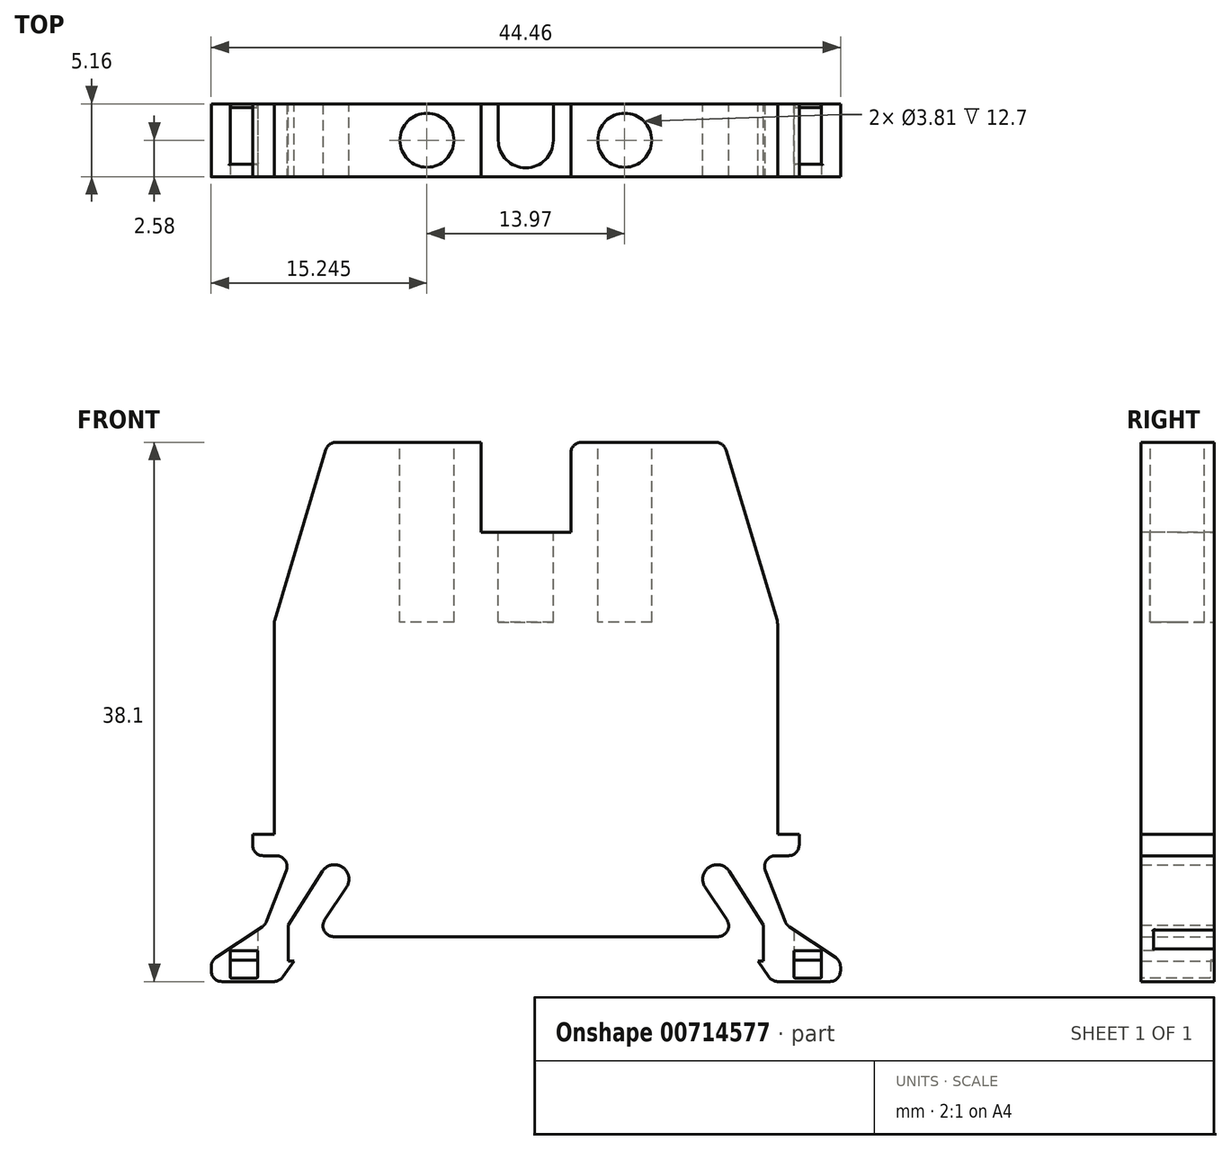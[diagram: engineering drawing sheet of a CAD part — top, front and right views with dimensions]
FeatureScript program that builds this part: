
annotation { "Feature Type Name" : "Feature", "Feature Type Description" : "" }
export const myFeature = defineFeature(function(context is Context, id is Id, definition is map)
    precondition{}
    {
        {
            var Q0;
            Q0=qCreatedBy(makeId("Front.planeOp"),FACE);
            var sketch = newSketch(context, id + "F0", { "sketchPlane" : qUnion([Q0])});
            skLineSegment(sketch, "E0", {"start": v(-13.97, 38.1) * mm, "end": v(13.97, 38.1) * mm});
            skLineSegment(sketch, "E1", {"start": v(0, 38.1) * mm, "end": v(0, 0) * mm, "construction": true});
            skLineSegment(sketch, "E2", {"start": v(-17.78, 25.4) * mm, "end": v(17.78, 25.4) * mm, "construction": true});
            skPoint(sketch, "E3", {"position": v(0, 25.4) * mm});
            skLineSegment(sketch, "E4", {"start": v(-17.78, 25.4) * mm, "end": v(-13.97, 38.1) * mm});
            skLineSegment(sketch, "E5", {"start": v(13.97, 38.1) * mm, "end": v(17.78, 25.4) * mm});
            skLineSegment(sketch, "E6", {"start": v(17.78, 8.9) * mm, "end": v(-17.78, 8.9) * mm});
            skLineSegment(sketch, "E7", {"start": v(17.78, 8.9) * mm, "end": v(19.3, 8.9) * mm});
            skLineSegment(sketch, "E8", {"start": v(19.3, 8.89) * mm, "end": v(19.3, 10.41) * mm});
            skLineSegment(sketch, "E9", {"start": v(19.3, 10.41) * mm, "end": v(17.78, 10.41) * mm});
            skLineSegment(sketch, "E10", {"start": v(17.78, 10.41) * mm, "end": v(17.78, 25.4) * mm});
            skLineSegment(sketch, "E11", {"start": v(-17.78, 8.9) * mm, "end": v(-19.3, 8.9) * mm});
            skLineSegment(sketch, "E12", {"start": v(-19.3, 8.89) * mm, "end": v(-19.3, 10.41) * mm});
            skLineSegment(sketch, "E13", {"start": v(-19.3, 10.41) * mm, "end": v(-17.78, 10.41) * mm});
            skLineSegment(sketch, "E14", {"start": v(-17.78, 10.41) * mm, "end": v(-17.78, 25.4) * mm});
            skLineSegment(sketch, "E15", {"start": v(-18.41, 4) * mm, "end": v(18.41, 4) * mm, "construction": true});
            skPoint(sketch, "E16", {"position": v(0, 4) * mm});
            skLineSegment(sketch, "E17", {"start": v(16.5, 8.89) * mm, "end": v(18.41, 4) * mm});
            skLineSegment(sketch, "E18", {"start": v(-18.41, 4) * mm, "end": v(-16.5, 8.89) * mm});
            skLineSegment(sketch, "E19", {"start": v(-16.51, 8.9) * mm, "end": v(16.51, 8.9) * mm, "construction": true});
            skPoint(sketch, "E20", {"position": v(0, 8.9) * mm});
            skLineSegment(sketch, "E21", {"start": v(-22.23, 1.46) * mm, "end": v(22.23, 1.46) * mm, "construction": true});
            skPoint(sketch, "E22", {"position": v(0, 1.46) * mm});
            skLineSegment(sketch, "E23", {"start": v(-18.41, 4) * mm, "end": v(-22.22, 1.46) * mm});
            skLineSegment(sketch, "E24", {"start": v(-22.23, 1.46) * mm, "end": v(-22.23, 0) * mm});
            skLineSegment(sketch, "E25", {"start": v(-22.23, 0) * mm, "end": v(-17.4, 0) * mm});
            skLineSegment(sketch, "E26", {"start": v(18.41, 4) * mm, "end": v(22.22, 1.46) * mm});
            skLineSegment(sketch, "E27", {"start": v(22.23, 1.46) * mm, "end": v(22.23, 0) * mm});
            skLineSegment(sketch, "E28", {"start": v(-14.99, 3.17) * mm, "end": v(14.99, 3.18) * mm});
            skPoint(sketch, "E29", {"position": v(0, 3.17) * mm});
            skLineSegment(sketch, "E30", {"start": v(-13.51, 7.24) * mm, "end": v(13.51, 7.24) * mm});
            skPoint(sketch, "E31", {"position": v(0, 7.24) * mm});
            skArc(sketch, "E32", {"start": v(-12.67, 6.68) * mm, "mid": v(-12.96, 8.1) * mm, "end": v(-14.37, 7.78) * mm});
            skArc(sketch, "E33", {"start": v(14.37, 7.78) * mm, "mid": v(12.96, 8.1) * mm, "end": v(12.67, 6.68) * mm});
            skLineSegment(sketch, "E34", {"start": v(-14.99, 3.17) * mm, "end": v(-12.67, 6.68) * mm});
            skLineSegment(sketch, "E35", {"start": v(14.99, 3.18) * mm, "end": v(12.67, 6.68) * mm});
            skLineSegment(sketch, "E36", {"start": v(-18.41, 4) * mm, "end": v(-16.76, 4) * mm, "construction": true});
            skLineSegment(sketch, "E37", {"start": v(-16.76, 4) * mm, "end": v(-14.37, 7.78) * mm});
            skLineSegment(sketch, "E38", {"start": v(18.41, 4) * mm, "end": v(16.76, 4) * mm});
            skLineSegment(sketch, "E39", {"start": v(14.37, 7.78) * mm, "end": v(16.76, 4) * mm});
            skLineSegment(sketch, "E40", {"start": v(22.23, 0) * mm, "end": v(17.4, 0) * mm});
            skLineSegment(sketch, "E41", {"start": v(17.4, 0) * mm, "end": v(16.38, 1.46) * mm});
            skLineSegment(sketch, "E42", {"start": v(16.38, 1.46) * mm, "end": v(16.76, 1.46) * mm});
            skLineSegment(sketch, "E43", {"start": v(16.76, 1.46) * mm, "end": v(16.76, 4) * mm});
            skLineSegment(sketch, "E44", {"start": v(-17.4, 0) * mm, "end": v(-16.38, 1.46) * mm});
            skLineSegment(sketch, "E45", {"start": v(-16.38, 1.46) * mm, "end": v(-16.76, 1.46) * mm});
            skLineSegment(sketch, "E46", {"start": v(-16.76, 1.46) * mm, "end": v(-16.76, 4) * mm});
            skSolve(sketch);
        }
        {
            var Q0;
            Q0 = qSketchRegion(id + "F0", true);
            extrude(context, id + "F1", {"entities" : qUnion([Q0]), "depth" : 5.16 * mm, "offsetDistance" : 25.4 * mm});
        }
        {
            var Q0;
            Q0=makeQuery(id+"F1.opExtrude","CAP_FACE",FACE,{"disambiguationData":[OSD([sQuery(id+"F0.wireOp",EDGE,"E0"),sQuery(id+"F0.wireOp",EDGE,"E4"),sQuery(id+"F0.wireOp",EDGE,"E5"),sQuery(id+"F0.wireOp",EDGE,"E6"),sQuery(id+"F0.wireOp",EDGE,"E7"),sQuery(id+"F0.wireOp",EDGE,"E8"),sQuery(id+"F0.wireOp",EDGE,"E9"),sQuery(id+"F0.wireOp",EDGE,"E10"),sQuery(id+"F0.wireOp",EDGE,"E11"),sQuery(id+"F0.wireOp",EDGE,"E12"),sQuery(id+"F0.wireOp",EDGE,"E13"),sQuery(id+"F0.wireOp",EDGE,"E14"),sQuery(id+"F0.wireOp",EDGE,"E17"),sQuery(id+"F0.wireOp",EDGE,"E18"),sQuery(id+"F0.wireOp",EDGE,"E23"),sQuery(id+"F0.wireOp",EDGE,"E24"),sQuery(id+"F0.wireOp",EDGE,"E25"),sQuery(id+"F0.wireOp",EDGE,"E26"),sQuery(id+"F0.wireOp",EDGE,"E27"),sQuery(id+"F0.wireOp",EDGE,"E28"),sQuery(id+"F0.wireOp",EDGE,"E32"),sQuery(id+"F0.wireOp",EDGE,"E33"),sQuery(id+"F0.wireOp",EDGE,"E34"),sQuery(id+"F0.wireOp",EDGE,"E35"),sQuery(id+"F0.wireOp",EDGE,"E37"),sQuery(id+"F0.wireOp",EDGE,"E39"),sQuery(id+"F0.wireOp",EDGE,"E40"),sQuery(id+"F0.wireOp",EDGE,"E41"),sQuery(id+"F0.wireOp",EDGE,"E42"),sQuery(id+"F0.wireOp",EDGE,"E43"),sQuery(id+"F0.wireOp",EDGE,"E44"),sQuery(id+"F0.wireOp",EDGE,"E45"),sQuery(id+"F0.wireOp",EDGE,"E46")])],"isStart":false});
            var sketch = newSketch(context, id + "F2", { "sketchPlane" : qUnion([Q0])});
            skLineSegment(sketch, "E47", {"start": v(-3.18, 38.1) * mm, "end": v(3.17, 38.1) * mm});
            skLineSegment(sketch, "E48", {"start": v(3.17, 38.1) * mm, "end": v(3.17, 31.75) * mm});
            skLineSegment(sketch, "E49", {"start": v(3.17, 31.75) * mm, "end": v(-3.18, 31.75) * mm});
            skLineSegment(sketch, "E50", {"start": v(-3.18, 31.75) * mm, "end": v(-3.18, 38.1) * mm});
            skPoint(sketch, "E51", {"position": v(0, 38.1) * mm});
            skLineSegment(sketch, "E52", {"start": v(-13.97, 38.1) * mm, "end": v(13.97, 38.1) * mm});
            skSolve(sketch);
        }
        {
            var Q0;
            Q0 = qSketchRegion(id + "F2", true);
            extrude(context, id + "F3", {"entities" : qUnion([Q0]), "operationType" : NewBodyOperationType.REMOVE, "oppositeDirection" : true, "depth" : 25.4 * mm, "offsetDistance" : 25.4 * mm});
        }
        {
            var Q0;
            {var subQ30=sQuery(id+"F0.wireOp",EDGE,"E5");var subQ32=sQuery(id+"F0.wireOp",EDGE,"E0");Q0=makeQuery(id+"F3.boolean.opBoolean","SPLIT",FACE,{"disambiguationData":[TD([makeQuery(id+"F1.opExtrude","SWEPT_FACE",FACE,{"disambiguationData":[OSD([subQ30])]})])],"derivedFrom":makeQuery(id+"F1.opExtrude","SWEPT_FACE",FACE,{"disambiguationData":[OSD([subQ32])]})});}
            var sketch = newSketch(context, id + "F4", { "sketchPlane" : qUnion([Q0])});
            skCircle(sketch, "E53", {"center": v(-6.99, -2.58) * mm, "radius": 1.9 * mm});
            skLineSegment(sketch, "E54", {"start": v(-13.97, -5.16) * mm, "end": v(-3.17, 0) * mm, "construction": true});
            skLineSegment(sketch, "E55", {"start": v(3.18, 0) * mm, "end": v(13.97, -5.16) * mm, "construction": true});
            skLineSegment(sketch, "E56", {"start": v(-8.57, -2.58) * mm, "end": v(-6.99, -2.58) * mm, "construction": true});
            skLineSegment(sketch, "E57", {"start": v(-6.99, -2.58) * mm, "end": v(6.99, -2.58) * mm, "construction": true});
            skLineSegment(sketch, "E58", {"start": v(6.99, -2.58) * mm, "end": v(8.57, -2.58) * mm, "construction": true});
            skCircle(sketch, "E59", {"center": v(6.99, -2.58) * mm, "radius": 1.9 * mm});
            skArc(sketch, "E60", {"start": v(-1.94, -2.58) * mm, "mid": v(0, -4.52) * mm, "end": v(1.94, -2.58) * mm});
            skLineSegment(sketch, "E61", {"start": v(-3.17, -5.16) * mm, "end": v(3.18, -5.16) * mm, "construction": true});
            skLineSegment(sketch, "E62", {"start": v(-1.94, -2.58) * mm, "end": v(-1.94, 0) * mm});
            skLineSegment(sketch, "E63", {"start": v(1.94, -2.58) * mm, "end": v(1.94, 0) * mm});
            skLineSegment(sketch, "E64", {"start": v(1.94, 0) * mm, "end": v(-1.94, 0) * mm});
            skSolve(sketch);
        }
        {
            var Q0;
            Q0 = qSketchRegion(id + "F4", true);
            extrude(context, id + "F5", {"entities" : qUnion([Q0]), "operationType" : NewBodyOperationType.REMOVE, "oppositeDirection" : true, "depth" : 12.7 * mm, "offsetDistance" : 25.4 * mm});
        }
        {
            var Q0;
            Q0=makeQuery(id+"F1.opExtrude","SWEPT_EDGE",EDGE,{"disambiguationData":[OSD([sQuery(id+"F0.wireOp",EDGE,"E0"),sQuery(id+"F0.wireOp",EDGE,"E5")])]});
            var Q1;
            Q1=makeQuery(id+"F1.opExtrude","SWEPT_EDGE",EDGE,{"disambiguationData":[OSD([sQuery(id+"F0.wireOp",EDGE,"E0"),sQuery(id+"F0.wireOp",EDGE,"E4")])]});
            var Q2;
            Q2=makeQuery(id+"F1.opExtrude","SWEPT_EDGE",EDGE,{"disambiguationData":[OSD([sQuery(id+"F0.wireOp",EDGE,"E5"),sQuery(id+"F0.wireOp",EDGE,"E10")])]});
            var Q3;
            Q3=makeQuery(id+"F1.opExtrude","SWEPT_EDGE",EDGE,{"disambiguationData":[OSD([sQuery(id+"F0.wireOp",EDGE,"E6"),sQuery(id+"F0.wireOp",EDGE,"E17")])]});
            var Q4;
            Q4=makeQuery(id+"F1.opExtrude","SWEPT_EDGE",EDGE,{"disambiguationData":[OSD([sQuery(id+"F0.wireOp",EDGE,"E7"),sQuery(id+"F0.wireOp",EDGE,"E8")])]});
            var Q5;
            Q5=makeQuery(id+"F1.opExtrude","SWEPT_EDGE",EDGE,{"disambiguationData":[OSD([sQuery(id+"F0.wireOp",EDGE,"E6"),sQuery(id+"F0.wireOp",EDGE,"E18")])]});
            var Q6;
            Q6=makeQuery(id+"F1.opExtrude","SWEPT_EDGE",EDGE,{"disambiguationData":[OSD([sQuery(id+"F0.wireOp",EDGE,"E11"),sQuery(id+"F0.wireOp",EDGE,"E12")])]});
            var Q7;
            Q7=makeQuery(id+"F1.opExtrude","SWEPT_EDGE",EDGE,{"disambiguationData":[OSD([sQuery(id+"F0.wireOp",EDGE,"E28"),sQuery(id+"F0.wireOp",EDGE,"E35")])]});
            var Q8;
            Q8=makeQuery(id+"F1.opExtrude","SWEPT_EDGE",EDGE,{"disambiguationData":[OSD([sQuery(id+"F0.wireOp",EDGE,"E28"),sQuery(id+"F0.wireOp",EDGE,"E34")])]});
            var Q9;
            Q9=makeQuery(id+"F1.opExtrude","SWEPT_EDGE",EDGE,{"disambiguationData":[OSD([sQuery(id+"F0.wireOp",EDGE,"E18"),sQuery(id+"F0.wireOp",EDGE,"E23")])]});
            var Q10;
            Q10=makeQuery(id+"F1.opExtrude","SWEPT_EDGE",EDGE,{"disambiguationData":[OSD([sQuery(id+"F0.wireOp",EDGE,"E23"),sQuery(id+"F0.wireOp",EDGE,"E24")])]});
            var Q11;
            Q11=makeQuery(id+"F1.opExtrude","SWEPT_EDGE",EDGE,{"disambiguationData":[OSD([sQuery(id+"F0.wireOp",EDGE,"E24"),sQuery(id+"F0.wireOp",EDGE,"E25")])]});
            var Q12;
            Q12=makeQuery(id+"F1.opExtrude","SWEPT_EDGE",EDGE,{"disambiguationData":[OSD([sQuery(id+"F0.wireOp",EDGE,"E27"),sQuery(id+"F0.wireOp",EDGE,"E40")])]});
            var Q13;
            Q13=makeQuery(id+"F1.opExtrude","SWEPT_EDGE",EDGE,{"disambiguationData":[OSD([sQuery(id+"F0.wireOp",EDGE,"E26"),sQuery(id+"F0.wireOp",EDGE,"E27")])]});
            var Q14;
            Q14=makeQuery(id+"F1.opExtrude","SWEPT_EDGE",EDGE,{"disambiguationData":[OSD([sQuery(id+"F0.wireOp",EDGE,"E17"),sQuery(id+"F0.wireOp",EDGE,"E26"),sQuery(id+"F0.wireOp",EDGE,"E38")])]});
            var Q15;
            Q15=makeQuery(id+"F1.opExtrude","SWEPT_EDGE",EDGE,{"disambiguationData":[OSD([sQuery(id+"F0.wireOp",EDGE,"E40"),sQuery(id+"F0.wireOp",EDGE,"E41")])]});
            var Q16;
            Q16=makeQuery(id+"F1.opExtrude","SWEPT_EDGE",EDGE,{"disambiguationData":[OSD([sQuery(id+"F0.wireOp",EDGE,"E25"),sQuery(id+"F0.wireOp",EDGE,"E44")])]});
            var Q17;
            Q17=makeQuery(id+"F3.boolean.opBoolean","COPY",EDGE,{"derivedFrom":makeQuery(id+"F3.opExtrude","SWEPT_EDGE",EDGE,{"disambiguationData":[OSD([sQuery(id+"F2.wireOp",EDGE,"E48"),sQuery(id+"F2.wireOp",EDGE,"E52")])]})});
            var Q18;
            Q18=makeQuery(id+"F3.boolean.opBoolean","COPY",EDGE,{"derivedFrom":makeQuery(id+"F3.opExtrude","SWEPT_EDGE",EDGE,{"disambiguationData":[OSD([sQuery(id+"F2.wireOp",EDGE,"E50"),sQuery(id+"F2.wireOp",EDGE,"E52")])]})});
            var Q19;
            Q19=makeQuery(id+"F1.opExtrude","SWEPT_EDGE",EDGE,{"disambiguationData":[OSD([sQuery(id+"F0.wireOp",EDGE,"E4"),sQuery(id+"F0.wireOp",EDGE,"E14")])]});
            fillet(context, id + "F6", {"entities" : qUnion([Q0, Q1, Q2, Q3, Q4, Q5, Q6, Q7, Q8, Q9, Q10, Q11, Q12, Q13, Q14, Q15, Q16, Q17, Q18, Q19]), "radius" : 0.76 * mm, "tangentPropagation" : true, "allowEdgeOverflow" : false});
        }
        {
            var Q0;
            Q0=makeQuery(id+"F1.opExtrude","CAP_FACE",FACE,{"disambiguationData":[OSD([sQuery(id+"F0.wireOp",EDGE,"E0"),sQuery(id+"F0.wireOp",EDGE,"E4"),sQuery(id+"F0.wireOp",EDGE,"E5"),sQuery(id+"F0.wireOp",EDGE,"E6"),sQuery(id+"F0.wireOp",EDGE,"E7"),sQuery(id+"F0.wireOp",EDGE,"E8"),sQuery(id+"F0.wireOp",EDGE,"E9"),sQuery(id+"F0.wireOp",EDGE,"E10"),sQuery(id+"F0.wireOp",EDGE,"E11"),sQuery(id+"F0.wireOp",EDGE,"E12"),sQuery(id+"F0.wireOp",EDGE,"E13"),sQuery(id+"F0.wireOp",EDGE,"E14"),sQuery(id+"F0.wireOp",EDGE,"E17"),sQuery(id+"F0.wireOp",EDGE,"E18"),sQuery(id+"F0.wireOp",EDGE,"E23"),sQuery(id+"F0.wireOp",EDGE,"E24"),sQuery(id+"F0.wireOp",EDGE,"E25"),sQuery(id+"F0.wireOp",EDGE,"E26"),sQuery(id+"F0.wireOp",EDGE,"E27"),sQuery(id+"F0.wireOp",EDGE,"E28"),sQuery(id+"F0.wireOp",EDGE,"E32"),sQuery(id+"F0.wireOp",EDGE,"E33"),sQuery(id+"F0.wireOp",EDGE,"E34"),sQuery(id+"F0.wireOp",EDGE,"E35"),sQuery(id+"F0.wireOp",EDGE,"E37"),sQuery(id+"F0.wireOp",EDGE,"E39"),sQuery(id+"F0.wireOp",EDGE,"E40"),sQuery(id+"F0.wireOp",EDGE,"E41"),sQuery(id+"F0.wireOp",EDGE,"E42"),sQuery(id+"F0.wireOp",EDGE,"E43"),sQuery(id+"F0.wireOp",EDGE,"E44"),sQuery(id+"F0.wireOp",EDGE,"E45"),sQuery(id+"F0.wireOp",EDGE,"E46")])],"isStart":true});
            var sketch = newSketch(context, id + "F7", { "sketchPlane" : qUnion([Q0])});
            skLineSegment(sketch, "E65.bottom", {"start": v(-20.88, 4.06) * mm, "end": v(-18.95, 4.06) * mm});
            skLineSegment(sketch, "E65.top", {"start": v(-20.88, 1.52) * mm, "end": v(-18.95, 1.52) * mm});
            skLineSegment(sketch, "E65.left", {"start": v(-20.88, 4.06) * mm, "end": v(-20.88, 1.52) * mm});
            skLineSegment(sketch, "E65.right", {"start": v(-18.95, 4.06) * mm, "end": v(-18.95, 1.52) * mm});
            skLineSegment(sketch, "E66.bottom", {"start": v(18.95, 4.06) * mm, "end": v(20.88, 4.06) * mm});
            skLineSegment(sketch, "E66.top", {"start": v(18.95, 1.52) * mm, "end": v(20.88, 1.52) * mm});
            skLineSegment(sketch, "E66.left", {"start": v(18.95, 4.06) * mm, "end": v(18.95, 1.52) * mm});
            skLineSegment(sketch, "E66.right", {"start": v(20.88, 4.06) * mm, "end": v(20.88, 1.52) * mm});
            skSolve(sketch);
        }
        {
            var Q0;
            Q0 = qSketchRegion(id + "F7", true);
            extrude(context, id + "F8", {"entities" : qUnion([Q0]), "operationType" : NewBodyOperationType.REMOVE, "oppositeDirection" : true, "depth" : 4.26 * mm, "offsetDistance" : 25.4 * mm});
        }
        {
            var Q0;
            Q0 = qSketchRegion(id + "F7", true);
            extrude(context, id + "F9", {"entities" : qUnion([Q0]), "operationType" : NewBodyOperationType.REMOVE, "oppositeDirection" : true, "depth" : 4.26 * mm, "offsetDistance" : 25.4 * mm});
        }
        {
            var Q0;
            Q0=makeQuery(id+"F1.opExtrude","CAP_FACE",FACE,{"disambiguationData":[OSD([sQuery(id+"F0.wireOp",EDGE,"E0"),sQuery(id+"F0.wireOp",EDGE,"E4"),sQuery(id+"F0.wireOp",EDGE,"E5"),sQuery(id+"F0.wireOp",EDGE,"E6"),sQuery(id+"F0.wireOp",EDGE,"E7"),sQuery(id+"F0.wireOp",EDGE,"E8"),sQuery(id+"F0.wireOp",EDGE,"E9"),sQuery(id+"F0.wireOp",EDGE,"E10"),sQuery(id+"F0.wireOp",EDGE,"E11"),sQuery(id+"F0.wireOp",EDGE,"E12"),sQuery(id+"F0.wireOp",EDGE,"E13"),sQuery(id+"F0.wireOp",EDGE,"E14"),sQuery(id+"F0.wireOp",EDGE,"E17"),sQuery(id+"F0.wireOp",EDGE,"E18"),sQuery(id+"F0.wireOp",EDGE,"E23"),sQuery(id+"F0.wireOp",EDGE,"E24"),sQuery(id+"F0.wireOp",EDGE,"E25"),sQuery(id+"F0.wireOp",EDGE,"E26"),sQuery(id+"F0.wireOp",EDGE,"E27"),sQuery(id+"F0.wireOp",EDGE,"E28"),sQuery(id+"F0.wireOp",EDGE,"E32"),sQuery(id+"F0.wireOp",EDGE,"E33"),sQuery(id+"F0.wireOp",EDGE,"E34"),sQuery(id+"F0.wireOp",EDGE,"E35"),sQuery(id+"F0.wireOp",EDGE,"E37"),sQuery(id+"F0.wireOp",EDGE,"E39"),sQuery(id+"F0.wireOp",EDGE,"E40"),sQuery(id+"F0.wireOp",EDGE,"E41"),sQuery(id+"F0.wireOp",EDGE,"E42"),sQuery(id+"F0.wireOp",EDGE,"E43"),sQuery(id+"F0.wireOp",EDGE,"E44"),sQuery(id+"F0.wireOp",EDGE,"E45"),sQuery(id+"F0.wireOp",EDGE,"E46")])],"isStart":false});
            var sketch = newSketch(context, id + "F10", { "sketchPlane" : qUnion([Q0])});
            skLineSegment(sketch, "E67.bottom", {"start": v(-20.88, 2.18) * mm, "end": v(-18.95, 2.18) * mm});
            skLineSegment(sketch, "E67.top", {"start": v(-20.88, 0.25) * mm, "end": v(-18.95, 0.25) * mm});
            skLineSegment(sketch, "E67.left", {"start": v(-20.88, 2.18) * mm, "end": v(-20.88, 0.25) * mm});
            skLineSegment(sketch, "E67.right", {"start": v(-18.95, 2.18) * mm, "end": v(-18.95, 0.25) * mm});
            skLineSegment(sketch, "E68.bottom", {"start": v(18.95, 2.18) * mm, "end": v(20.88, 2.18) * mm});
            skLineSegment(sketch, "E68.top", {"start": v(18.95, 0.25) * mm, "end": v(20.88, 0.25) * mm});
            skLineSegment(sketch, "E68.left", {"start": v(18.95, 2.18) * mm, "end": v(18.95, 0.25) * mm});
            skLineSegment(sketch, "E68.right", {"start": v(20.88, 2.18) * mm, "end": v(20.88, 0.25) * mm});
            skSolve(sketch);
        }
        {
            var Q0;
            Q0 = qSketchRegion(id + "F10", true);
            extrude(context, id + "F11", {"entities" : qUnion([Q0]), "operationType" : NewBodyOperationType.REMOVE, "oppositeDirection" : true, "depth" : 4.9 * mm, "offsetDistance" : 25.4 * mm});
        }
        {
            var Q0;
            Q0=makeQuery(id+"F8.boolean.opBoolean","COPY",EDGE,{"derivedFrom":makeQuery(id+"F8.opExtrude","CAP_EDGE",EDGE,{"disambiguationData":[OSD([sQuery(id+"F7.wireOp",EDGE,"E65.right")])],"isStart":false})});
            var Q1;
            Q1=makeQuery(id+"F8.boolean.opBoolean","INTERSECT",EDGE,{"derivedFrom":[makeQuery(id+"F1.opExtrude","SWEPT_FACE",FACE,{"disambiguationData":[OSD([sQuery(id+"F0.wireOp",EDGE,"E26")])]}),makeQuery(id+"F8.opExtrude","CAP_FACE",FACE,{"disambiguationData":[OSD([sQuery(id+"F7.wireOp",EDGE,"E65.bottom"),sQuery(id+"F7.wireOp",EDGE,"E65.top"),sQuery(id+"F7.wireOp",EDGE,"E65.left"),sQuery(id+"F7.wireOp",EDGE,"E65.right")])],"isStart":false})]});
            var Q2;
            Q2=makeQuery(id+"F8.boolean.opBoolean","INTERSECT",EDGE,{"derivedFrom":[makeQuery(id+"F1.opExtrude","SWEPT_FACE",FACE,{"disambiguationData":[OSD([sQuery(id+"F0.wireOp",EDGE,"E26")])]}),makeQuery(id+"F8.opExtrude","SWEPT_FACE",FACE,{"disambiguationData":[OSD([sQuery(id+"F7.wireOp",EDGE,"E65.left")])]})]});
            var Q3;
            Q3=makeQuery(id+"F8.boolean.opBoolean","COPY",EDGE,{"derivedFrom":makeQuery(id+"F8.opExtrude","CAP_EDGE",EDGE,{"disambiguationData":[OSD([sQuery(id+"F7.wireOp",EDGE,"E65.left")])],"isStart":true})});
            var Q4;
            Q4=makeQuery(id+"F8.boolean.opBoolean","COPY",EDGE,{"derivedFrom":makeQuery(id+"F8.opExtrude","CAP_EDGE",EDGE,{"disambiguationData":[OSD([sQuery(id+"F7.wireOp",EDGE,"E65.top")])],"isStart":true})});
            var Q5;
            Q5=makeQuery(id+"F11.boolean.opBoolean","INTERSECT",EDGE,{"derivedFrom":[makeQuery(id+"F8.boolean.opBoolean","COPY",FACE,{"derivedFrom":makeQuery(id+"F8.opExtrude","SWEPT_FACE",FACE,{"disambiguationData":[OSD([sQuery(id+"F7.wireOp",EDGE,"E65.top")])]})}),makeQuery(id+"F11.opExtrude","CAP_FACE",FACE,{"disambiguationData":[OSD([sQuery(id+"F10.wireOp",EDGE,"E68.bottom"),sQuery(id+"F10.wireOp",EDGE,"E68.top"),sQuery(id+"F10.wireOp",EDGE,"E68.left"),sQuery(id+"F10.wireOp",EDGE,"E68.right")])],"isStart":false})]});
            var Q6;
            Q6=makeQuery(id+"F8.boolean.opBoolean","COPY",EDGE,{"derivedFrom":makeQuery(id+"F8.opExtrude","CAP_EDGE",EDGE,{"disambiguationData":[OSD([sQuery(id+"F7.wireOp",EDGE,"E65.right")])],"isStart":true})});
            var Q7;
            Q7=makeQuery(id+"F11.boolean.opBoolean","COPY",EDGE,{"derivedFrom":makeQuery(id+"F11.opExtrude","SWEPT_EDGE",EDGE,{"disambiguationData":[OSD([sQuery(id+"F10.wireOp",EDGE,"E68.top"),sQuery(id+"F10.wireOp",EDGE,"E68.left")])]})});
            var Q8;
            Q8=makeQuery(id+"F11.boolean.opBoolean","COPY",EDGE,{"derivedFrom":makeQuery(id+"F11.opExtrude","CAP_EDGE",EDGE,{"disambiguationData":[OSD([sQuery(id+"F10.wireOp",EDGE,"E68.top")])],"isStart":false})});
            var Q9;
            Q9=makeQuery(id+"F11.boolean.opBoolean","COPY",EDGE,{"derivedFrom":makeQuery(id+"F11.opExtrude","CAP_EDGE",EDGE,{"disambiguationData":[OSD([sQuery(id+"F10.wireOp",EDGE,"E68.left")])],"isStart":false})});
            var Q10;
            Q10=makeQuery(id+"F11.boolean.opBoolean","COPY",EDGE,{"derivedFrom":makeQuery(id+"F11.opExtrude","CAP_EDGE",EDGE,{"disambiguationData":[OSD([sQuery(id+"F10.wireOp",EDGE,"E68.right")])],"isStart":false})});
            var Q11;
            Q11=makeQuery(id+"F11.boolean.opBoolean","COPY",EDGE,{"derivedFrom":makeQuery(id+"F11.opExtrude","SWEPT_EDGE",EDGE,{"disambiguationData":[OSD([sQuery(id+"F10.wireOp",EDGE,"E68.top"),sQuery(id+"F10.wireOp",EDGE,"E68.right")])]})});
            var Q12;
            Q12=makeQuery(id+"F11.boolean.opBoolean","COPY",EDGE,{"derivedFrom":makeQuery(id+"F11.opExtrude","CAP_EDGE",EDGE,{"disambiguationData":[OSD([sQuery(id+"F10.wireOp",EDGE,"E68.bottom")])],"isStart":true})});
            var Q13;
            Q13=makeQuery(id+"F8.boolean.opBoolean","COPY",EDGE,{"derivedFrom":makeQuery(id+"F8.opExtrude","CAP_EDGE",EDGE,{"disambiguationData":[OSD([sQuery(id+"F7.wireOp",EDGE,"E66.top")])],"isStart":true})});
            var Q14;
            Q14=makeQuery(id+"F11.boolean.opBoolean","INTERSECT",EDGE,{"derivedFrom":[makeQuery(id+"F8.boolean.opBoolean","COPY",FACE,{"derivedFrom":makeQuery(id+"F8.opExtrude","SWEPT_FACE",FACE,{"disambiguationData":[OSD([sQuery(id+"F7.wireOp",EDGE,"E66.top")])]})}),makeQuery(id+"F11.opExtrude","CAP_FACE",FACE,{"disambiguationData":[OSD([sQuery(id+"F10.wireOp",EDGE,"E67.bottom"),sQuery(id+"F10.wireOp",EDGE,"E67.top"),sQuery(id+"F10.wireOp",EDGE,"E67.left"),sQuery(id+"F10.wireOp",EDGE,"E67.right")])],"isStart":false})]});
            var Q15;
            Q15=makeQuery(id+"F8.boolean.opBoolean","COPY",EDGE,{"derivedFrom":makeQuery(id+"F8.opExtrude","CAP_EDGE",EDGE,{"disambiguationData":[OSD([sQuery(id+"F7.wireOp",EDGE,"E66.left")])],"isStart":false})});
            var Q16;
            Q16=makeQuery(id+"F8.boolean.opBoolean","INTERSECT",EDGE,{"derivedFrom":[makeQuery(id+"F1.opExtrude","SWEPT_FACE",FACE,{"disambiguationData":[OSD([sQuery(id+"F0.wireOp",EDGE,"E23")])]}),makeQuery(id+"F8.opExtrude","CAP_FACE",FACE,{"disambiguationData":[OSD([sQuery(id+"F7.wireOp",EDGE,"E66.bottom"),sQuery(id+"F7.wireOp",EDGE,"E66.top"),sQuery(id+"F7.wireOp",EDGE,"E66.left"),sQuery(id+"F7.wireOp",EDGE,"E66.right")])],"isStart":false})]});
            var Q17;
            Q17=makeQuery(id+"F11.boolean.opBoolean","COPY",EDGE,{"derivedFrom":makeQuery(id+"F11.opExtrude","CAP_EDGE",EDGE,{"disambiguationData":[OSD([sQuery(id+"F10.wireOp",EDGE,"E67.bottom")])],"isStart":true})});
            var Q18;
            Q18=makeQuery(id+"F11.boolean.opBoolean","COPY",EDGE,{"derivedFrom":makeQuery(id+"F11.opExtrude","CAP_EDGE",EDGE,{"disambiguationData":[OSD([sQuery(id+"F10.wireOp",EDGE,"E67.top")])],"isStart":false})});
            var Q19;
            Q19=makeQuery(id+"F11.boolean.opBoolean","COPY",EDGE,{"derivedFrom":makeQuery(id+"F11.opExtrude","CAP_EDGE",EDGE,{"disambiguationData":[OSD([sQuery(id+"F10.wireOp",EDGE,"E67.left")])],"isStart":false})});
            var Q20;
            Q20=makeQuery(id+"F11.boolean.opBoolean","COPY",EDGE,{"derivedFrom":makeQuery(id+"F11.opExtrude","SWEPT_EDGE",EDGE,{"disambiguationData":[OSD([sQuery(id+"F10.wireOp",EDGE,"E67.top"),sQuery(id+"F10.wireOp",EDGE,"E67.left")])]})});
            var Q21;
            Q21=makeQuery(id+"F11.boolean.opBoolean","COPY",EDGE,{"derivedFrom":makeQuery(id+"F11.opExtrude","SWEPT_EDGE",EDGE,{"disambiguationData":[OSD([sQuery(id+"F10.wireOp",EDGE,"E67.top"),sQuery(id+"F10.wireOp",EDGE,"E67.right")])]})});
            var Q22;
            Q22=makeQuery(id+"F11.boolean.opBoolean","COPY",EDGE,{"derivedFrom":makeQuery(id+"F11.opExtrude","CAP_EDGE",EDGE,{"disambiguationData":[OSD([sQuery(id+"F10.wireOp",EDGE,"E67.right")])],"isStart":false})});
            var Q23;
            Q23=makeQuery(id+"F8.boolean.opBoolean","INTERSECT",EDGE,{"derivedFrom":[makeQuery(id+"F1.opExtrude","SWEPT_FACE",FACE,{"disambiguationData":[OSD([sQuery(id+"F0.wireOp",EDGE,"E23")])]}),makeQuery(id+"F8.opExtrude","SWEPT_FACE",FACE,{"disambiguationData":[OSD([sQuery(id+"F7.wireOp",EDGE,"E66.right")])]})]});
            fillet(context, id + "F12", {"entities" : qUnion([Q0, Q1, Q2, Q3, Q4, Q5, Q6, Q7, Q8, Q9, Q10, Q11, Q12, Q13, Q14, Q15, Q16, Q17, Q18, Q19, Q20, Q21, Q22, Q23]), "radius" : 0.06 * mm, "tangentPropagation" : true, "allowEdgeOverflow" : false});
        }
    });
